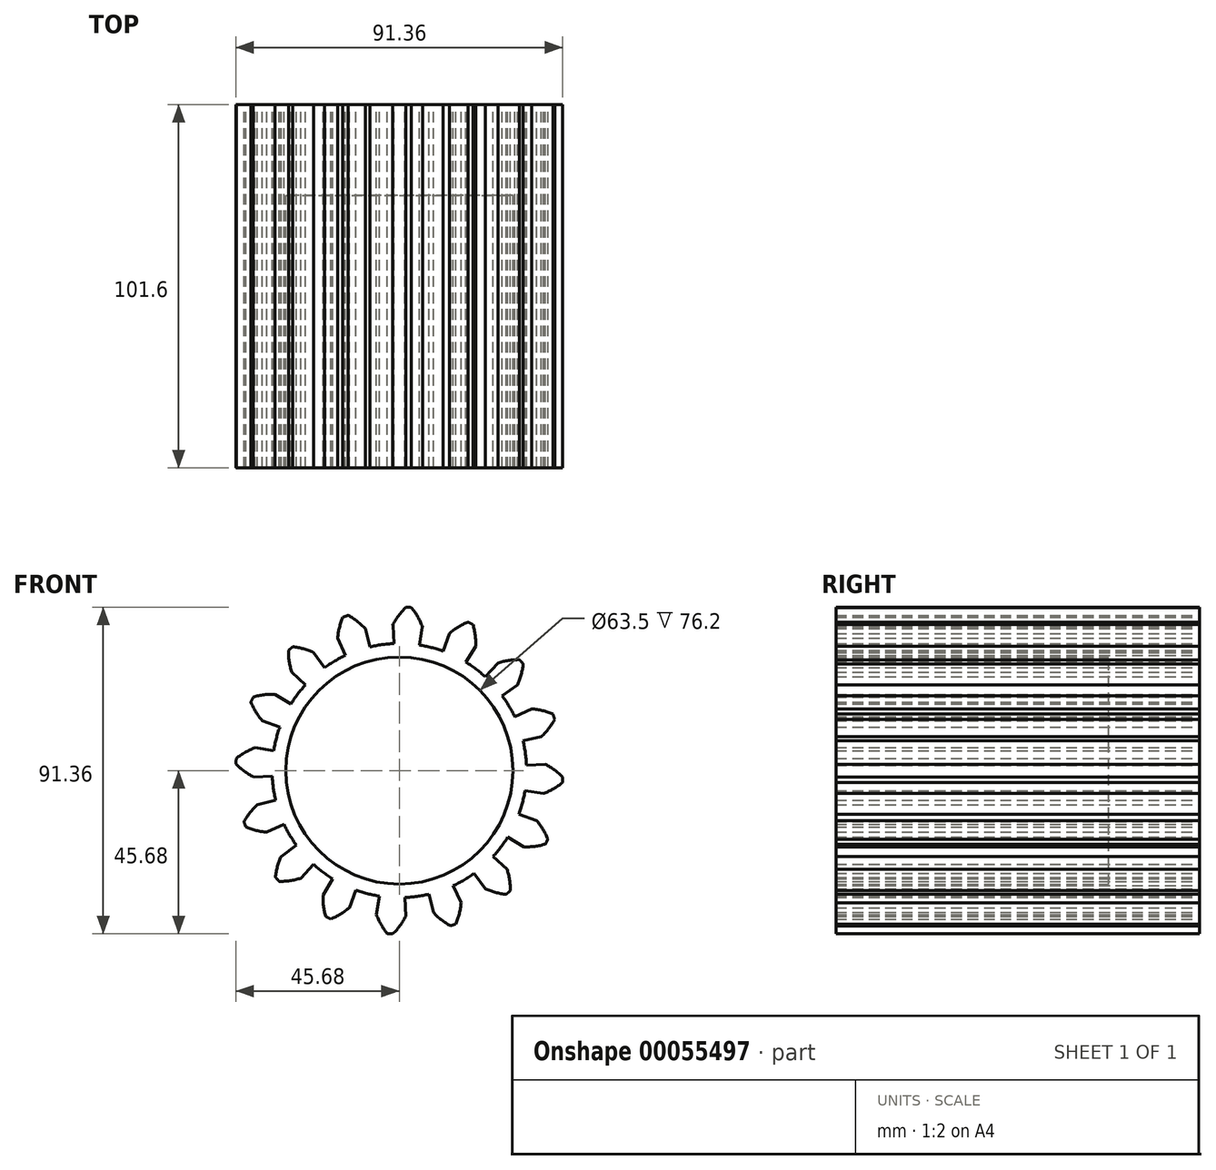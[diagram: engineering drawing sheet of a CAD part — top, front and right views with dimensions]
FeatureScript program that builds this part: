
annotation { "Feature Type Name" : "Feature", "Feature Type Description" : "" }
export const myFeature = defineFeature(function(context is Context, id is Id, definition is map)
    precondition{}
    {
        {
            var Q0;
            Q0=qCreatedBy(makeId("Front.planeOp"),FACE);
            var sketch = newSketch(context, id + "F0", { "sketchPlane" : qUnion([Q0])});
            skArc(sketch, "E0", {"start": v(3.38, 45.6) * mm, "mid": v(2.6, 45.65) * mm, "end": v(1.83, 45.68) * mm});
            skArc(sketch, "E1", {"start": v(-26.21, 24.03) * mm, "mid": v(-28.4, 21.4) * mm, "end": v(-30.31, 18.6) * mm});
            skArc(sketch, "E2", {"start": v(6.47, 40.12) * mm, "mid": v(6.42, 40.13) * mm, "end": v(6.37, 40.14) * mm});
            skPoint(sketch, "E3.orphan", {"position": v(-51.95, 40.14) * mm});
            skArc(sketch, "E4.trimOffspring", {"start": v(6.47, 40.12) * mm, "mid": v(5.16, 42.99) * mm, "end": v(3.38, 45.6) * mm});
            skPoint(sketch, "E5.trimOffspring.end.orphan", {"position": v(-51.95, 18.9) * mm});
            skLineSegment(sketch, "E6.trimOffspring", {"start": v(5.58, 35.12) * mm, "end": v(6.4, 40.31) * mm});
            skPoint(sketch, "E7.trimOffspring.end.orphan", {"position": v(8.62, 54.27) * mm});
            skPoint(sketch, "E8.trimOffspring.end.orphan", {"position": v(-2.11, 54.27) * mm});
            skArc(sketch, "E9.MirrorCS", {"start": v(-1.87, 40.6) * mm, "mid": v(-0.23, 43.3) * mm, "end": v(1.83, 45.68) * mm});
            skLineSegment(sketch, "E10.MirrorCS", {"start": v(-1.55, 35.53) * mm, "end": v(-1.77, 40.78) * mm});
            skArc(sketch, "E11.trimOffspring", {"start": v(-1.77, 40.6) * mm, "mid": v(-1.82, 40.6) * mm, "end": v(-1.87, 40.6) * mm});
            skArc(sketch, "E12.1.0", {"start": v(-17.26, 36.8) * mm, "mid": v(-16.78, 39.91) * mm, "end": v(-15.8, 42.9) * mm});
            skLineSegment(sketch, "E12.1.1", {"start": v(-15.02, 32.23) * mm, "end": v(-17.24, 37) * mm});
            skLineSegment(sketch, "E12.1.2", {"start": v(-8.29, 34.58) * mm, "end": v(-9.51, 39.7) * mm});
            skArc(sketch, "E12.1.3", {"start": v(-9.38, 39.54) * mm, "mid": v(-11.69, 41.69) * mm, "end": v(-14.32, 43.42) * mm});
            skArc(sketch, "E12.1.4", {"start": v(-14.32, 43.42) * mm, "mid": v(-15.06, 43.17) * mm, "end": v(-15.8, 42.9) * mm});
            skArc(sketch, "E12.2.0", {"start": v(-30.03, 27.39) * mm, "mid": v(-30.78, 30.45) * mm, "end": v(-31.01, 33.6) * mm});
            skLineSegment(sketch, "E12.2.1", {"start": v(-26.21, 24.03) * mm, "end": v(-30.09, 27.58) * mm});
            skLineSegment(sketch, "E12.2.2", {"start": v(-20.9, 28.78) * mm, "end": v(-23.98, 33.03) * mm});
            skArc(sketch, "E12.2.3", {"start": v(-23.8, 32.95) * mm, "mid": v(-26.75, 34.04) * mm, "end": v(-29.85, 34.63) * mm});
            skArc(sketch, "E12.2.4", {"start": v(-29.85, 34.63) * mm, "mid": v(-30.43, 34.12) * mm, "end": v(-31.01, 33.6) * mm});
            skArc(sketch, "E12.3.0", {"start": v(-38.22, 13.81) * mm, "mid": v(-40.09, 16.35) * mm, "end": v(-41.5, 19.17) * mm});
            skLineSegment(sketch, "E12.3.1", {"start": v(-33.41, 12.17) * mm, "end": v(-38.35, 13.97) * mm});
            skLineSegment(sketch, "E12.3.2", {"start": v(-30.31, 18.6) * mm, "end": v(-34.8, 21.34) * mm});
            skArc(sketch, "E12.3.3", {"start": v(-34.6, 21.33) * mm, "mid": v(-37.74, 21.22) * mm, "end": v(-40.83, 20.57) * mm});
            skArc(sketch, "E12.3.4", {"start": v(-40.83, 20.57) * mm, "mid": v(-41.17, 19.87) * mm, "end": v(-41.5, 19.17) * mm});
            skArc(sketch, "E12.4.0", {"start": v(-40.6, -1.87) * mm, "mid": v(-43.3, -0.23) * mm, "end": v(-45.68, 1.83) * mm});
            skLineSegment(sketch, "E12.4.1", {"start": v(-35.53, -1.55) * mm, "end": v(-40.78, -1.77) * mm});
            skLineSegment(sketch, "E12.4.2", {"start": v(-35.12, 5.58) * mm, "end": v(-40.31, 6.4) * mm});
            skArc(sketch, "E12.4.3", {"start": v(-40.12, 6.47) * mm, "mid": v(-42.99, 5.16) * mm, "end": v(-45.6, 3.38) * mm});
            skArc(sketch, "E12.4.4", {"start": v(-45.6, 3.38) * mm, "mid": v(-45.65, 2.6) * mm, "end": v(-45.68, 1.83) * mm});
            skArc(sketch, "E12.5.0", {"start": v(-36.8, -17.26) * mm, "mid": v(-39.91, -16.78) * mm, "end": v(-42.9, -15.8) * mm});
            skLineSegment(sketch, "E12.5.1", {"start": v(-32.23, -15.02) * mm, "end": v(-37, -17.24) * mm});
            skLineSegment(sketch, "E12.5.2", {"start": v(-34.58, -8.29) * mm, "end": v(-39.7, -9.51) * mm});
            skArc(sketch, "E12.5.3", {"start": v(-39.54, -9.38) * mm, "mid": v(-41.69, -11.69) * mm, "end": v(-43.42, -14.32) * mm});
            skArc(sketch, "E12.5.4", {"start": v(-43.42, -14.32) * mm, "mid": v(-43.17, -15.06) * mm, "end": v(-42.9, -15.8) * mm});
            skArc(sketch, "E12.6.0", {"start": v(-27.39, -30.03) * mm, "mid": v(-30.45, -30.78) * mm, "end": v(-33.6, -31.01) * mm});
            skLineSegment(sketch, "E12.6.1", {"start": v(-24.03, -26.21) * mm, "end": v(-27.58, -30.09) * mm});
            skLineSegment(sketch, "E12.6.2", {"start": v(-28.78, -20.9) * mm, "end": v(-33.03, -23.98) * mm});
            skArc(sketch, "E12.6.3", {"start": v(-32.95, -23.8) * mm, "mid": v(-34.04, -26.75) * mm, "end": v(-34.63, -29.85) * mm});
            skArc(sketch, "E12.6.4", {"start": v(-34.63, -29.85) * mm, "mid": v(-34.12, -30.43) * mm, "end": v(-33.6, -31.01) * mm});
            skArc(sketch, "E12.7.0", {"start": v(-13.81, -38.22) * mm, "mid": v(-16.35, -40.09) * mm, "end": v(-19.17, -41.5) * mm});
            skLineSegment(sketch, "E12.7.1", {"start": v(-12.17, -33.41) * mm, "end": v(-13.97, -38.35) * mm});
            skLineSegment(sketch, "E12.7.2", {"start": v(-18.6, -30.31) * mm, "end": v(-21.34, -34.8) * mm});
            skArc(sketch, "E12.7.3", {"start": v(-21.33, -34.6) * mm, "mid": v(-21.22, -37.74) * mm, "end": v(-20.57, -40.83) * mm});
            skArc(sketch, "E12.7.4", {"start": v(-20.57, -40.83) * mm, "mid": v(-19.87, -41.17) * mm, "end": v(-19.17, -41.5) * mm});
            skArc(sketch, "E12.8.0", {"start": v(1.87, -40.6) * mm, "mid": v(0.23, -43.3) * mm, "end": v(-1.83, -45.68) * mm});
            skLineSegment(sketch, "E12.8.1", {"start": v(1.55, -35.53) * mm, "end": v(1.77, -40.78) * mm});
            skLineSegment(sketch, "E12.8.2", {"start": v(-5.58, -35.12) * mm, "end": v(-6.4, -40.31) * mm});
            skArc(sketch, "E12.8.3", {"start": v(-6.47, -40.12) * mm, "mid": v(-5.16, -42.99) * mm, "end": v(-3.38, -45.6) * mm});
            skArc(sketch, "E12.8.4", {"start": v(-3.38, -45.6) * mm, "mid": v(-2.6, -45.65) * mm, "end": v(-1.83, -45.68) * mm});
            skArc(sketch, "E12.9.0", {"start": v(17.26, -36.8) * mm, "mid": v(16.78, -39.91) * mm, "end": v(15.8, -42.9) * mm});
            skLineSegment(sketch, "E12.9.1", {"start": v(15.02, -32.23) * mm, "end": v(17.24, -37) * mm});
            skLineSegment(sketch, "E12.9.2", {"start": v(8.29, -34.58) * mm, "end": v(9.51, -39.7) * mm});
            skArc(sketch, "E12.9.3", {"start": v(9.38, -39.54) * mm, "mid": v(11.69, -41.69) * mm, "end": v(14.32, -43.42) * mm});
            skArc(sketch, "E12.9.4", {"start": v(14.32, -43.42) * mm, "mid": v(15.06, -43.17) * mm, "end": v(15.8, -42.9) * mm});
            skArc(sketch, "E12.10.0", {"start": v(30.03, -27.39) * mm, "mid": v(30.78, -30.45) * mm, "end": v(31.01, -33.6) * mm});
            skLineSegment(sketch, "E12.10.1", {"start": v(26.21, -24.03) * mm, "end": v(30.09, -27.58) * mm});
            skLineSegment(sketch, "E12.10.2", {"start": v(20.9, -28.78) * mm, "end": v(23.98, -33.03) * mm});
            skArc(sketch, "E12.10.3", {"start": v(23.8, -32.95) * mm, "mid": v(26.75, -34.04) * mm, "end": v(29.85, -34.63) * mm});
            skArc(sketch, "E12.10.4", {"start": v(29.85, -34.63) * mm, "mid": v(30.43, -34.12) * mm, "end": v(31.01, -33.6) * mm});
            skArc(sketch, "E12.11.0", {"start": v(38.22, -13.81) * mm, "mid": v(40.09, -16.35) * mm, "end": v(41.5, -19.17) * mm});
            skLineSegment(sketch, "E12.11.1", {"start": v(33.41, -12.17) * mm, "end": v(38.35, -13.97) * mm});
            skLineSegment(sketch, "E12.11.2", {"start": v(30.31, -18.6) * mm, "end": v(34.8, -21.34) * mm});
            skArc(sketch, "E12.11.3", {"start": v(34.6, -21.33) * mm, "mid": v(37.74, -21.22) * mm, "end": v(40.83, -20.57) * mm});
            skArc(sketch, "E12.11.4", {"start": v(40.83, -20.57) * mm, "mid": v(41.17, -19.87) * mm, "end": v(41.5, -19.17) * mm});
            skArc(sketch, "E12.12.0", {"start": v(40.6, 1.87) * mm, "mid": v(43.3, 0.23) * mm, "end": v(45.68, -1.83) * mm});
            skLineSegment(sketch, "E12.12.1", {"start": v(35.53, 1.55) * mm, "end": v(40.78, 1.77) * mm});
            skLineSegment(sketch, "E12.12.2", {"start": v(35.12, -5.58) * mm, "end": v(40.31, -6.4) * mm});
            skArc(sketch, "E12.12.3", {"start": v(40.12, -6.47) * mm, "mid": v(42.99, -5.16) * mm, "end": v(45.6, -3.38) * mm});
            skArc(sketch, "E12.12.4", {"start": v(45.6, -3.38) * mm, "mid": v(45.65, -2.6) * mm, "end": v(45.68, -1.83) * mm});
            skArc(sketch, "E12.13.0", {"start": v(36.8, 17.26) * mm, "mid": v(39.91, 16.78) * mm, "end": v(42.9, 15.8) * mm});
            skLineSegment(sketch, "E12.13.1", {"start": v(32.23, 15.02) * mm, "end": v(37, 17.24) * mm});
            skLineSegment(sketch, "E12.13.2", {"start": v(34.58, 8.29) * mm, "end": v(39.7, 9.51) * mm});
            skArc(sketch, "E12.13.3", {"start": v(39.54, 9.38) * mm, "mid": v(41.69, 11.69) * mm, "end": v(43.42, 14.32) * mm});
            skArc(sketch, "E12.13.4", {"start": v(43.42, 14.32) * mm, "mid": v(43.17, 15.06) * mm, "end": v(42.9, 15.8) * mm});
            skArc(sketch, "E12.14.0", {"start": v(27.39, 30.03) * mm, "mid": v(30.45, 30.78) * mm, "end": v(33.6, 31.01) * mm});
            skLineSegment(sketch, "E12.14.1", {"start": v(24.03, 26.21) * mm, "end": v(27.58, 30.09) * mm});
            skLineSegment(sketch, "E12.14.2", {"start": v(28.78, 20.9) * mm, "end": v(33.03, 23.98) * mm});
            skArc(sketch, "E12.14.3", {"start": v(32.95, 23.8) * mm, "mid": v(34.04, 26.75) * mm, "end": v(34.63, 29.85) * mm});
            skArc(sketch, "E12.14.4", {"start": v(34.63, 29.85) * mm, "mid": v(34.12, 30.43) * mm, "end": v(33.6, 31.01) * mm});
            skArc(sketch, "E12.15.0", {"start": v(13.81, 38.22) * mm, "mid": v(16.35, 40.09) * mm, "end": v(19.17, 41.5) * mm});
            skLineSegment(sketch, "E12.15.1", {"start": v(12.17, 33.41) * mm, "end": v(13.97, 38.35) * mm});
            skLineSegment(sketch, "E12.15.2", {"start": v(18.6, 30.31) * mm, "end": v(21.34, 34.8) * mm});
            skArc(sketch, "E12.15.3", {"start": v(21.33, 34.6) * mm, "mid": v(21.22, 37.74) * mm, "end": v(20.57, 40.83) * mm});
            skArc(sketch, "E12.15.4", {"start": v(20.57, 40.83) * mm, "mid": v(19.87, 41.17) * mm, "end": v(19.17, 41.5) * mm});
            skArc(sketch, "E13.trimOffspring", {"start": v(-33.41, 12.17) * mm, "mid": v(-34.42, 8.91) * mm, "end": v(-35.12, 5.58) * mm});
            skArc(sketch, "E14.trimOffspring", {"start": v(-35.53, -1.55) * mm, "mid": v(-35.22, -4.94) * mm, "end": v(-34.58, -8.29) * mm});
            skArc(sketch, "E15.trimOffspring", {"start": v(-15.02, 32.23) * mm, "mid": v(-18.04, 30.64) * mm, "end": v(-20.9, 28.78) * mm});
            skArc(sketch, "E16.trimOffspring", {"start": v(-1.55, 35.53) * mm, "mid": v(-4.94, 35.22) * mm, "end": v(-8.29, 34.58) * mm});
            skArc(sketch, "E17.trimOffspring", {"start": v(12.17, 33.41) * mm, "mid": v(8.91, 34.42) * mm, "end": v(5.58, 35.12) * mm});
            skArc(sketch, "E18.trimOffspring", {"start": v(24.03, 26.21) * mm, "mid": v(21.4, 28.4) * mm, "end": v(18.6, 30.31) * mm});
            skArc(sketch, "E19.trimOffspring", {"start": v(32.23, 15.02) * mm, "mid": v(30.64, 18.04) * mm, "end": v(28.78, 20.9) * mm});
            skArc(sketch, "E20.trimOffspring", {"start": v(35.53, 1.55) * mm, "mid": v(35.22, 4.94) * mm, "end": v(34.58, 8.29) * mm});
            skArc(sketch, "E21.trimOffspring", {"start": v(33.41, -12.17) * mm, "mid": v(34.42, -8.91) * mm, "end": v(35.12, -5.58) * mm});
            skArc(sketch, "E22.trimOffspring", {"start": v(26.21, -24.03) * mm, "mid": v(28.4, -21.4) * mm, "end": v(30.31, -18.6) * mm});
            skArc(sketch, "E23.trimOffspring", {"start": v(15.02, -32.23) * mm, "mid": v(18.04, -30.64) * mm, "end": v(20.9, -28.78) * mm});
            skArc(sketch, "E24.trimOffspring", {"start": v(1.55, -35.53) * mm, "mid": v(4.94, -35.22) * mm, "end": v(8.29, -34.58) * mm});
            skArc(sketch, "E25.trimOffspring", {"start": v(-12.17, -33.41) * mm, "mid": v(-8.91, -34.42) * mm, "end": v(-5.58, -35.12) * mm});
            skArc(sketch, "E26.trimOffspring", {"start": v(-24.03, -26.21) * mm, "mid": v(-21.4, -28.4) * mm, "end": v(-18.6, -30.31) * mm});
            skArc(sketch, "E27.trimOffspring", {"start": v(-32.23, -15.02) * mm, "mid": v(-30.64, -18.04) * mm, "end": v(-28.78, -20.9) * mm});
            skCircle(sketch, "E28", {"center": v(0, 0) * mm, "radius": 31.75 * mm});
            skSolve(sketch);
        }
        {
            var Q0;
            Q0 = qSketchRegion(id + "F0", true);
            extrude(context, id + "F1", {"entities" : qUnion([Q0]), "depth" : 101.6 * mm});
        }
        {
            var Q0;
            Q0=qCreatedBy(makeId("Front.planeOp"),FACE);
            var sketch = newSketch(context, id + "F2", { "sketchPlane" : qUnion([Q0])});
            skCircle(sketch, "E29", {"center": v(0, 0) * mm, "radius": 31.75 * mm});
            skSolve(sketch);
        }
        {
            var Q0;
            Q0=makeQuery(id+"F2.imprint","IMPRINT",FACE,{"disambiguationData":[TD([[makeQuery(id+"F2.imprint","IMPRINT",EDGE,{"derivedFrom":sQuery(id+"F2.wireOp",EDGE,"E29")}),1.0]])]});
            extrude(context, id + "F3", {"entities" : qUnion([Q0]), "operationType" : NewBodyOperationType.ADD, "depth" : 25.4 * mm});
        }
    });
